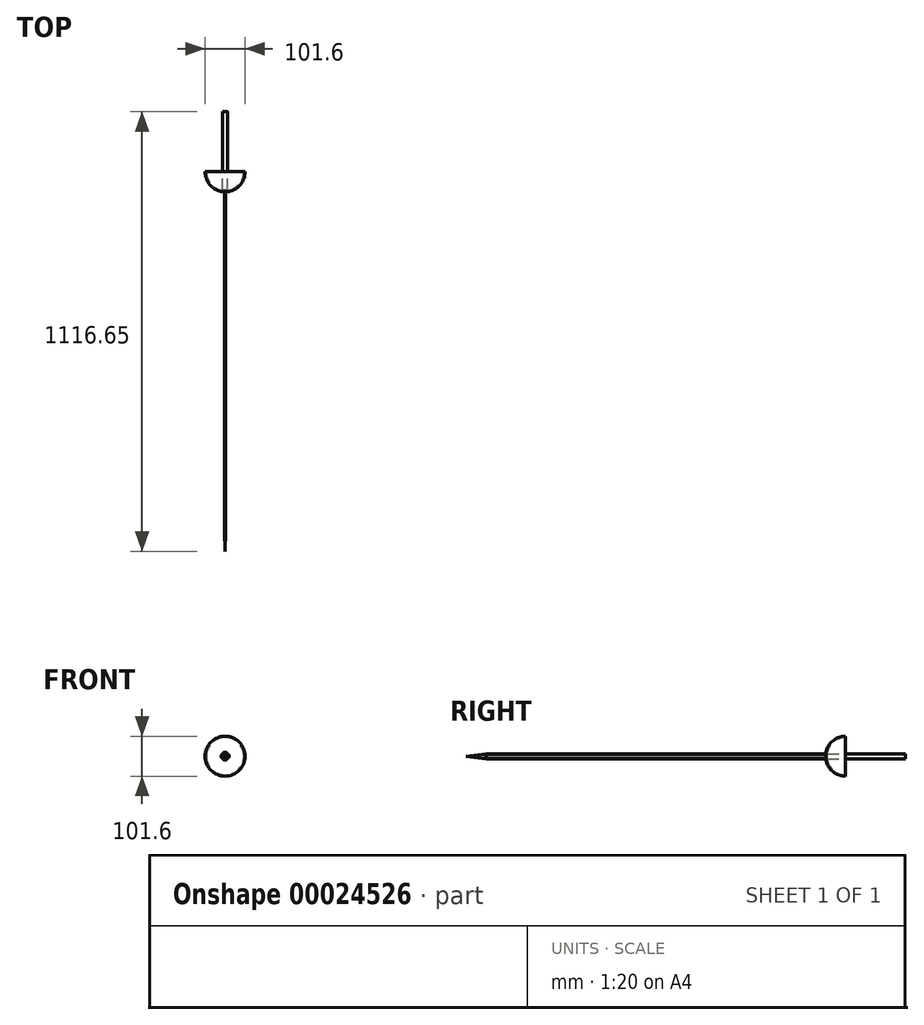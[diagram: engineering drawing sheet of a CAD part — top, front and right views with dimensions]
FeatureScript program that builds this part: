
annotation { "Feature Type Name" : "Feature", "Feature Type Description" : "" }
export const myFeature = defineFeature(function(context is Context, id is Id, definition is map)
    precondition{}
    {
        {
            var Q0;
            Q0=qCreatedBy(makeId("Front.planeOp"),FACE);
            var sketch = newSketch(context, id + "F0", { "sketchPlane" : qUnion([Q0])});
            skCircle(sketch, "E0", {"center": v(0, 0) * mm, "radius": 6.35 * mm});
            skSolve(sketch);
        }
        {
            var Q0;
            Q0=makeQuery(id+"F0.imprint","IMPRINT",FACE,{"disambiguationData":[TD([[makeQuery(id+"F0.imprint","IMPRINT",EDGE,{"derivedFrom":sQuery(id+"F0.wireOp",EDGE,"E0")}),1.0]])]});
            extrude(context, id + "F1", {"entities" : qUnion([Q0]), "depth" : 152.4 * mm, "offsetDistance" : 25.4 * mm});
        }
        {
            var Q0;
            Q0=makeQuery(id+"F1.opExtrude","CAP_FACE",FACE,{"disambiguationData":[OSD([sQuery(id+"F0.wireOp",EDGE,"E0")])],"isStart":false});
            var sketch = newSketch(context, id + "F2", { "sketchPlane" : qUnion([Q0])});
            skCircle(sketch, "E1", {"center": v(0, 0) * mm, "radius": 50.8 * mm});
            skCircle(sketch, "E2", {"center": v(0, 0) * mm, "radius": 47.63 * mm});
            skLineSegment(sketch, "E3", {"start": v(47.63, 0) * mm, "end": v(50.8, 0) * mm});
            skLineSegment(sketch, "E4", {"start": v(0, 0) * mm, "end": v(47.63, 0) * mm});
            skLineSegment(sketch, "E5", {"start": v(0, 0) * mm, "end": v(-50.8, 0) * mm});
            skSolve(sketch);
        }
        {
            var Q0;
            {var subQ0=sQuery(id+"F2.wireOp",EDGE,"E3");Q0=makeQuery(id+"F2.imprint","IMPRINT",FACE,{"disambiguationData":[TD([[makeQuery(id+"F2.imprint","IMPRINT",EDGE,{"derivedFrom":subQ0}),1.0]])]});}
            var Q1;
            Q1=sQuery(id+"F2.wireOp",EDGE,"E4");
            revolve(context, id + "F3", {"surfaceOperationType" : NewSurfaceOperationType.NEW, "entities" : qUnion([Q0]), "axis" : qUnion([Q1]), "revolveType" : RevolveType.ONE_DIRECTION, "angle" : 180 * degree});
        }
        {
            var Q0;
            Q0=makeQuery(id+"F1.opExtrude","CAP_FACE",FACE,{"disambiguationData":[OSD([sQuery(id+"F0.wireOp",EDGE,"E0")])],"isStart":false});
            extrude(context, id + "F4", {"entities" : qUnion([Q0]), "operationType" : NewBodyOperationType.ADD, "depth" : 52.4 * mm, "offsetDistance" : 25.4 * mm});
        }
        {
            var Q0;
            Q0=makeQuery(id+"F4.opExtrude","CAP_FACE",FACE,{"disambiguationData":[OSD([sQuery(id+"F0.wireOp",EDGE,"E0")])],"isStart":false});
            var sketch = newSketch(context, id + "F5", { "sketchPlane" : qUnion([Q0])});
            skLineSegment(sketch, "E6", {"start": v(0, 0) * mm, "end": v(0, 12.7) * mm});
            skLineSegment(sketch, "E7", {"start": v(0, 0) * mm, "end": v(-12.7, 0) * mm});
            skLineSegment(sketch, "E8", {"start": v(0, 0) * mm, "end": v(0, -12.7) * mm});
            skLineSegment(sketch, "E9", {"start": v(0, 0) * mm, "end": v(12.7, 0) * mm});
            skLineSegment(sketch, "E10", {"start": v(0, 12.7) * mm, "end": v(-12.7, 0) * mm});
            skLineSegment(sketch, "E11", {"start": v(-12.7, 0) * mm, "end": v(0, -12.7) * mm});
            skLineSegment(sketch, "E12", {"start": v(12.7, 0) * mm, "end": v(0, -12.7) * mm});
            skLineSegment(sketch, "E13", {"start": v(12.7, 0) * mm, "end": v(0, 12.7) * mm});
            skSolve(sketch);
        }
        {
            var Q0;
            {var subQ0=sQuery(id+"F5.wireOp",EDGE,"E10");Q0=makeQuery(id+"F5.imprint","IMPRINT",FACE,{"disambiguationData":[TD([[makeQuery(id+"F5.imprint","IMPRINT",EDGE,{"derivedFrom":subQ0}),1.0]])]});}
            var Q1;
            {var subQ1=sQuery(id+"F5.wireOp",EDGE,"E6");var subQ3=makeQuery(id+"F4.opExtrude","CAP_EDGE",EDGE,{"disambiguationData":[OSD([sQuery(id+"F0.wireOp",EDGE,"E0")])],"isStart":false});var subQ4=makeQuery(id+"F5.imprint","INTERSECT",VERTEX,{"derivedFrom":[subQ3,subQ1]});Q1=makeQuery(id+"F5.imprint","IMPRINT",FACE,{"disambiguationData":[TD([[makeQuery(id+"F5.imprint","IMPRINT",EDGE,{"disambiguationData":[TD([[subQ4,1.0]])],"derivedFrom":subQ3}),1.0]])]});}
            var Q2;
            {var subQ1=sQuery(id+"F5.wireOp",EDGE,"E8");var subQ3=makeQuery(id+"F4.opExtrude","CAP_EDGE",EDGE,{"disambiguationData":[OSD([sQuery(id+"F0.wireOp",EDGE,"E0")])],"isStart":false});var subQ4=makeQuery(id+"F5.imprint","INTERSECT",VERTEX,{"derivedFrom":[subQ3,subQ1]});Q2=makeQuery(id+"F5.imprint","IMPRINT",FACE,{"disambiguationData":[TD([[makeQuery(id+"F5.imprint","IMPRINT",EDGE,{"disambiguationData":[TD([[subQ4,-1.0]])],"derivedFrom":subQ3}),1.0]])]});}
            var Q3;
            {var subQ1=sQuery(id+"F5.wireOp",EDGE,"E6");var subQ3=makeQuery(id+"F4.opExtrude","CAP_EDGE",EDGE,{"disambiguationData":[OSD([sQuery(id+"F0.wireOp",EDGE,"E0")])],"isStart":false});var subQ4=makeQuery(id+"F5.imprint","INTERSECT",VERTEX,{"derivedFrom":[subQ3,subQ1]});Q3=makeQuery(id+"F5.imprint","IMPRINT",FACE,{"disambiguationData":[TD([[makeQuery(id+"F5.imprint","IMPRINT",EDGE,{"disambiguationData":[TD([[subQ4,-1.0]])],"derivedFrom":subQ3}),1.0]])]});}
            var Q4;
            {var subQ1=sQuery(id+"F5.wireOp",EDGE,"E7");var subQ3=makeQuery(id+"F4.opExtrude","CAP_EDGE",EDGE,{"disambiguationData":[OSD([sQuery(id+"F0.wireOp",EDGE,"E0")])],"isStart":false});var subQ4=makeQuery(id+"F5.imprint","INTERSECT",VERTEX,{"derivedFrom":[subQ3,subQ1]});Q4=makeQuery(id+"F5.imprint","IMPRINT",FACE,{"disambiguationData":[TD([[makeQuery(id+"F5.imprint","IMPRINT",EDGE,{"disambiguationData":[TD([[subQ4,-1.0]])],"derivedFrom":subQ3}),1.0]])]});}
            var Q5;
            {var subQ0=sQuery(id+"F5.wireOp",EDGE,"E11");Q5=makeQuery(id+"F5.imprint","IMPRINT",FACE,{"disambiguationData":[TD([[makeQuery(id+"F5.imprint","IMPRINT",EDGE,{"derivedFrom":subQ0}),1.0]])]});}
            var Q6;
            {var subQ0=sQuery(id+"F5.wireOp",EDGE,"E12");Q6=makeQuery(id+"F5.imprint","IMPRINT",FACE,{"disambiguationData":[TD([[makeQuery(id+"F5.imprint","IMPRINT",EDGE,{"derivedFrom":subQ0}),-1.0]])]});}
            var Q7;
            {var subQ0=sQuery(id+"F5.wireOp",EDGE,"E13");Q7=makeQuery(id+"F5.imprint","IMPRINT",FACE,{"disambiguationData":[TD([[makeQuery(id+"F5.imprint","IMPRINT",EDGE,{"derivedFrom":subQ0}),1.0]])]});}
            extrude(context, id + "F6", {"entities" : qUnion([Q0, Q1, Q2, Q3, Q4, Q5, Q6, Q7]), "operationType" : NewBodyOperationType.REMOVE, "oppositeDirection" : true, "depth" : 2.54 * mm, "offsetDistance" : 25.4 * mm});
        }
        {
            var Q0;
            Q0=makeQuery(id+"F6.boolean.opBoolean","COPY",FACE,{"derivedFrom":makeQuery(id+"F6.opExtrude","CAP_FACE",FACE,{"disambiguationData":[OSD([sQuery(id+"F5.wireOp",EDGE,"E10"),sQuery(id+"F5.wireOp",EDGE,"E11"),sQuery(id+"F5.wireOp",EDGE,"E12"),sQuery(id+"F5.wireOp",EDGE,"E13")])],"isStart":false})});
            var sketch = newSketch(context, id + "F7", { "sketchPlane" : qUnion([Q0])});
            skLineSegment(sketch, "E14", {"start": v(0, 0) * mm, "end": v(0, 6.35) * mm});
            skLineSegment(sketch, "E15", {"start": v(0, 0) * mm, "end": v(0, -6.35) * mm});
            skLineSegment(sketch, "E16", {"start": v(0, 6.35) * mm, "end": v(1.35, 5) * mm});
            skLineSegment(sketch, "E17", {"start": v(0, 6.35) * mm, "end": v(-1.35, 5) * mm});
            skLineSegment(sketch, "E18", {"start": v(0, -6.35) * mm, "end": v(-1.35, -5) * mm});
            skLineSegment(sketch, "E19", {"start": v(0, -6.35) * mm, "end": v(1.35, -5) * mm});
            skLineSegment(sketch, "E20", {"start": v(-1.35, 5) * mm, "end": v(-1.35, -5) * mm});
            skLineSegment(sketch, "E21", {"start": v(1.35, -5) * mm, "end": v(1.35, 5) * mm});
            skSolve(sketch);
        }
        {
            var Q0;
            Q0=makeQuery(id+"F7.imprint","IMPRINT",FACE,{"disambiguationData":[TD([[makeQuery(id+"F7.imprint","IMPRINT",EDGE,{"derivedFrom":sQuery(id+"F7.wireOp",EDGE,"E14")}),1.0]])]});
            var Q1;
            Q1=makeQuery(id+"F7.imprint","IMPRINT",FACE,{"disambiguationData":[TD([[makeQuery(id+"F7.imprint","IMPRINT",EDGE,{"derivedFrom":sQuery(id+"F7.wireOp",EDGE,"E14")}),-1.0]])]});
            extrude(context, id + "F8", {"entities" : qUnion([Q0, Q1]), "operationType" : NewBodyOperationType.ADD, "depth" : 863.6 * mm, "offsetDistance" : 25.4 * mm});
        }
        {
            var Q0;
            Q0=makeQuery(id+"F8.opExtrude","CAP_FACE",FACE,{"disambiguationData":[OSD([sQuery(id+"F7.wireOp",EDGE,"E16"),sQuery(id+"F7.wireOp",EDGE,"E17"),sQuery(id+"F7.wireOp",EDGE,"E18"),sQuery(id+"F7.wireOp",EDGE,"E19"),sQuery(id+"F7.wireOp",EDGE,"E20"),sQuery(id+"F7.wireOp",EDGE,"E21")])],"isStart":false});
            var sketch = newSketch(context, id + "F9", { "sketchPlane" : qUnion([Q0])});
            skLineSegment(sketch, "E22", {"start": v(1.35, 0) * mm, "end": v(0, 0) * mm});
            skSolve(sketch);
        }
        {
            var Q0;
            {var subQ1=makeQuery(id+"F8.opExtrude","CAP_EDGE",EDGE,{"disambiguationData":[OSD([sQuery(id+"F7.wireOp",EDGE,"E16")])],"isStart":false});Q0=makeQuery(id+"F9.imprint","IMPRINT",FACE,{"disambiguationData":[TD([[makeQuery(id+"F9.imprint","IMPRINT",EDGE,{"derivedFrom":subQ1}),-1.0]])]});}
            cPlane(context, id + "F10", {"entities" : qUnion([Q0]), "cplaneType" : CPlaneType.OFFSET, "offset" : 50.8 * mm, "width" : 152.4 * mm, "height" : 152.4 * mm});
        }
        {
            var Q0;
            Q0=qCreatedBy(id+"F10.planeOp",FACE);
            var sketch = newSketch(context, id + "F11", { "sketchPlane" : qUnion([Q0])});
            skPoint(sketch, "E23", {"position": v(0.06, -0.05) * mm});
            skSolve(sketch);
        }
        {
            var Q1;
            {var subQ1=makeQuery(id+"F8.opExtrude","CAP_EDGE",EDGE,{"disambiguationData":[OSD([sQuery(id+"F7.wireOp",EDGE,"E16")])],"isStart":false});Q1=makeQuery(id+"F9.imprint","IMPRINT",FACE,{"disambiguationData":[TD([[makeQuery(id+"F9.imprint","IMPRINT",EDGE,{"derivedFrom":subQ1}),-1.0]])]});}
            var Q2;
            Q2=sQuery(id+"F11.wireOp",VERTEX,"E23");
            loft(context, id + "F12", {"operationType" : NewBodyOperationType.ADD, "sheetProfilesArray" : [{ "sheetProfileEntities" : qUnion([Q1]) }, { "sheetProfileEntities" : qUnion([Q2]) }]});
        }
    });
